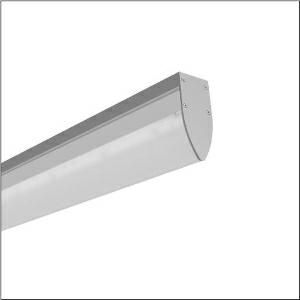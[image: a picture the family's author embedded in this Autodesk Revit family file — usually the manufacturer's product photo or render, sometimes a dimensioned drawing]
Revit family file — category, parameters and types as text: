
# Revit family: mira_r__21_td_51fr527k474a_9fa0
name_source: partatom
category: Lighting Fixtures
units: mm (PartAtom-declared; Revit-internal decimal feet)

## family parameters
Cut with Voids When Loaded = No
Host = Face
Light Source = No
Part Type = Normal
Room Calculation Point = No
Round Connector Dimension = Use Diameter
Shared = No

## types (1)
- Mira® 21 TD (1 x LED, 7330 lm, 52 W, 4000K)
    Apparent Load = 52 VA
    CIE Flux Codes = 40 68 87 81 100
    Color Rendering = 80
    Color Temperature = 4000K
    Default Elevation = 1800 mm
    Description = Mira® 21 TD, clean room luminaire, primary light control with reflector, primary optical cover: cover, of PMMA, frosted, light emission: direct distribution, primary light characteristic: symmetric, installation type: surface-mounted, LED, rated luminous flux: 7.330lm, luminous efficacy: 141lm/W, light colour: 840, colour temperature: 4000K, control gear: ECG, with terminal, 3-pole, max. 2.5mm², mains connection: 230V, AC, 50/60Hz, rated input power: 52W, luminaire housing, of sheet steel, coated, pure white, length: 1.200mm, width: 55mm, height: 120mm, protection rating (complete): IP43, insulation class (complete): insulation class I (protective earthing), certification: CE, UKCA, permissible operating ambient temperature: -5..+40°C, standard: EN 50419, packaging unit: 1 piece
    Height = 0 mm  [stored 0 ft]
    Lamp = 1 x LED
    Lamp Light Flux = 7330 lm
    Lamp Power = 52 W
    Lamp count = 1
    Length = 1200 mm
    Luminous efficacy = 141 lm/W
    Manufacturer = Siteco
    ModVariant = No
    Model = 51FR527K474A
    Mounting Place = Ceiling
    Mounting Type = Recessed
    Number of Poles = 1
    OnlyDefault = Yes
    Power Factor = 1
    Product Name = Mira® 21 TD
    Product group = clean room luminaire
    ProductGroupID = 401
    Protection Class = Protection class I
    Protection Degree = IP 43
    RLX_Detail_Level = 1
    RlxData = <blob elided: 25121 chars, md5=d31ed5f8>
    Socket = socket
    Standby Power = 0 W
    System Light Flux = 7330 lm
    System Power = 52 W
    Type Comments = Product without accessories
    Type Image = l_1007115.jpg
    URL = http://relux.com
    VarID = ---
    Voltage = 0 V
    Weight = 0.00 kg
    Width = 55 mm

note: [stored X ft] marks values corroborated as IEEE doubles in the binary element streams (Revit-internal decimal feet)

## geometry (parser evidence)
native form markers: Blend x4, Sweep x12
no freeform markers — native parametric forms only
